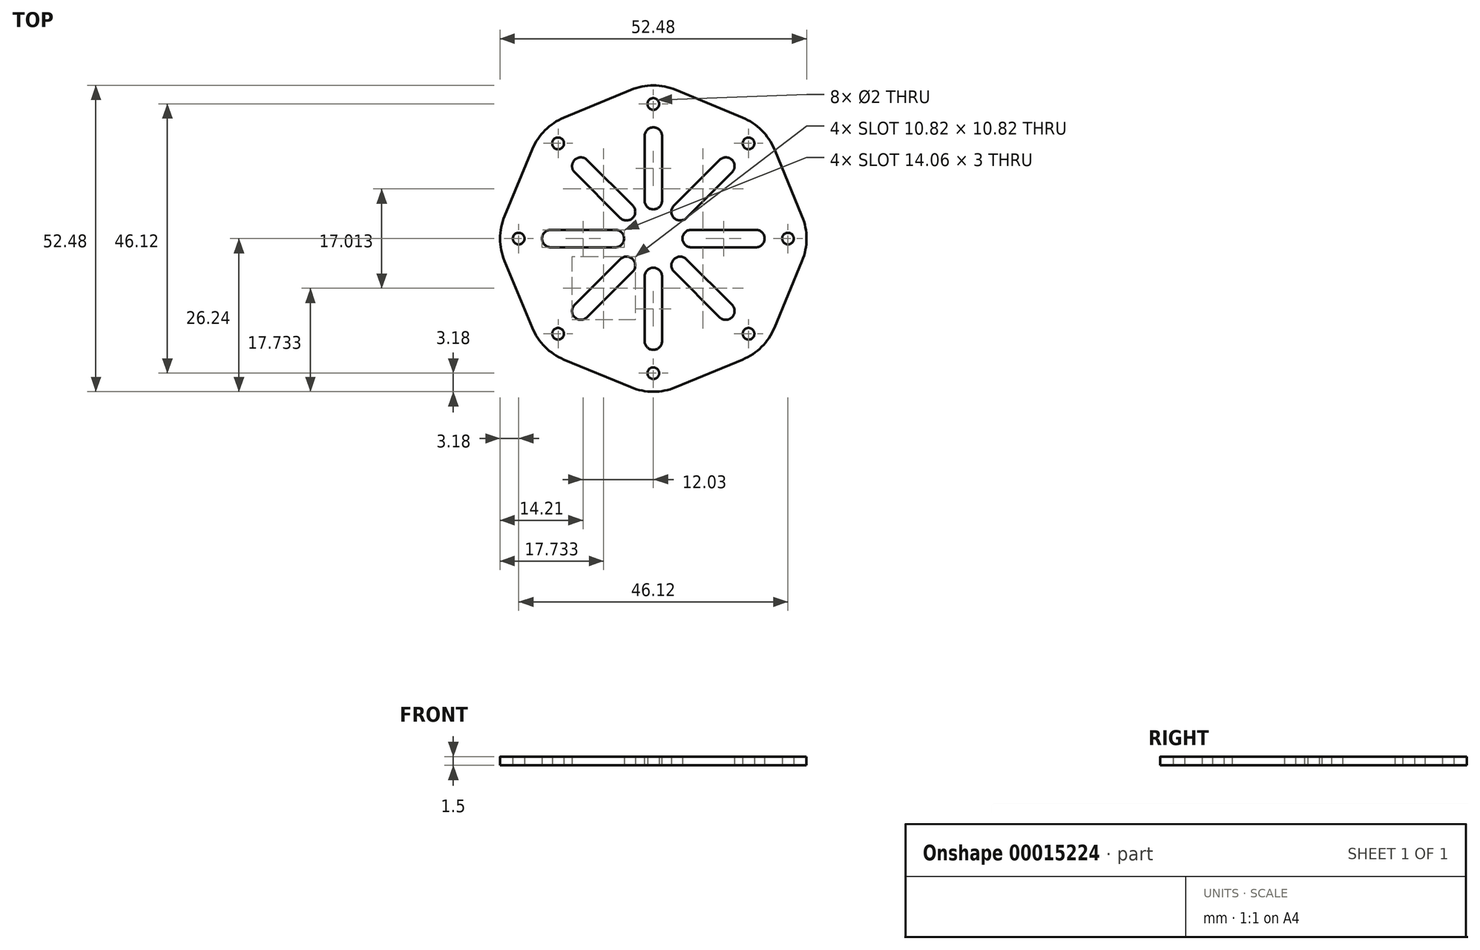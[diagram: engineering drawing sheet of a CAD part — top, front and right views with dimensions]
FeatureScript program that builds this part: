
annotation { "Feature Type Name" : "Feature", "Feature Type Description" : "" }
export const myFeature = defineFeature(function(context is Context, id is Id, definition is map)
    precondition{}
    {
        {
            var Q0;
            Q0=qCreatedBy(makeId("Top.planeOp"),FACE);
            var sketch = newSketch(context, id + "F0", { "sketchPlane" : qUnion([Q0])});
            skCircle(sketch, "E0.cCircle", {"center": v(0, 0) * mm, "radius": 25 * mm, "construction": true});
            skLineSegment(sketch, "E0.0", {"start": v(19.13, 19.13) * mm, "end": v(27.06, 0) * mm});
            skLineSegment(sketch, "E0.1", {"start": v(27.06, 0) * mm, "end": v(19.13, -19.13) * mm});
            skLineSegment(sketch, "E0.2", {"start": v(19.13, -19.13) * mm, "end": v(0, -27.06) * mm});
            skLineSegment(sketch, "E0.3", {"start": v(0, -27.06) * mm, "end": v(-19.13, -19.13) * mm});
            skLineSegment(sketch, "E0.4", {"start": v(-19.13, -19.13) * mm, "end": v(-27.06, 0) * mm});
            skLineSegment(sketch, "E0.5", {"start": v(-27.06, 0) * mm, "end": v(-19.13, 19.13) * mm});
            skLineSegment(sketch, "E0.6", {"start": v(-19.13, 19.13) * mm, "end": v(0, 27.06) * mm});
            skLineSegment(sketch, "E0.7", {"start": v(0, 27.06) * mm, "end": v(19.13, 19.13) * mm});
            skPoint(sketch, "E0.0.midPoint", {"position": v(23.1, 9.57) * mm});
            skPoint(sketch, "E1", {"position": v(0, -23.06) * mm});
            skPoint(sketch, "E2.1.0", {"position": v(16.3, -16.3) * mm});
            skPoint(sketch, "E2.2.0", {"position": v(23.06, 0) * mm});
            skPoint(sketch, "E2.3.0", {"position": v(16.3, 16.3) * mm});
            skPoint(sketch, "E2.4.0", {"position": v(0, 23.06) * mm});
            skPoint(sketch, "E2.5.0", {"position": v(-16.3, 16.3) * mm});
            skPoint(sketch, "E2.6.0", {"position": v(-23.06, 0) * mm});
            skPoint(sketch, "E2.7.0", {"position": v(-16.3, -16.3) * mm});
            skCircle(sketch, "E3", {"center": v(0, 0) * mm, "radius": 19.06 * mm});
            skLineSegment(sketch, "E4", {"start": v(0, 19.06) * mm, "end": v(0, 23.06) * mm, "construction": true});
            skLineSegment(sketch, "E5", {"start": v(0, 23.06) * mm, "end": v(0, 27.06) * mm, "construction": true});
            skCircle(sketch, "E6", {"center": v(0, 0) * mm, "radius": 5 * mm});
            skLineSegment(sketch, "E7", {"start": v(-13.48, -13.48) * mm, "end": v(-3.54, -3.54) * mm});
            skLineSegment(sketch, "E8", {"start": v(19.06, 0) * mm, "end": v(5, 0) * mm});
            skLineSegment(sketch, "E9", {"start": v(0, 19.06) * mm, "end": v(0, 5) * mm});
            skLineSegment(sketch, "E10", {"start": v(13.48, -13.48) * mm, "end": v(3.54, -3.54) * mm});
            skLineSegment(sketch, "E11.trimOffspring", {"start": v(3.54, 3.54) * mm, "end": v(13.48, 13.48) * mm});
            skLineSegment(sketch, "E12.trimOffspring", {"start": v(-5, 0) * mm, "end": v(-19.06, 0) * mm});
            skLineSegment(sketch, "E13.trimOffspring", {"start": v(-3.54, 3.54) * mm, "end": v(-13.48, 13.48) * mm});
            skLineSegment(sketch, "E14.trimOffspring", {"start": v(0, -5) * mm, "end": v(0, -19.06) * mm});
            skSolve(sketch);
        }
        {
            var Q0;
            Q0=makeQuery(id+"F0.imprint","IMPRINT",FACE,{"disambiguationData":[TD([[makeQuery(id+"F0.imprint","IMPRINT",EDGE,{"derivedFrom":sQuery(id+"F0.wireOp",EDGE,"E0.0")}),-1.0]])]});
            var Q1;
            {var subQ1=sQuery(id+"F0.wireOp",EDGE,"E7");Q1=makeQuery(id+"F0.imprint","IMPRINT",FACE,{"disambiguationData":[TD([[makeQuery(id+"F0.imprint","IMPRINT",EDGE,{"derivedFrom":subQ1}),1.0]])]});}
            var Q2;
            {var subQ1=sQuery(id+"F0.wireOp",EDGE,"E7");Q2=makeQuery(id+"F0.imprint","IMPRINT",FACE,{"disambiguationData":[TD([[makeQuery(id+"F0.imprint","IMPRINT",EDGE,{"derivedFrom":subQ1}),-1.0]])]});}
            var Q3;
            {var subQ1=sQuery(id+"F0.wireOp",EDGE,"E10");Q3=makeQuery(id+"F0.imprint","IMPRINT",FACE,{"disambiguationData":[TD([[makeQuery(id+"F0.imprint","IMPRINT",EDGE,{"derivedFrom":subQ1}),1.0]])]});}
            var Q4;
            {var subQ1=sQuery(id+"F0.wireOp",EDGE,"E8");Q4=makeQuery(id+"F0.imprint","IMPRINT",FACE,{"disambiguationData":[TD([[makeQuery(id+"F0.imprint","IMPRINT",EDGE,{"derivedFrom":subQ1}),1.0]])]});}
            var Q5;
            {var subQ1=sQuery(id+"F0.wireOp",EDGE,"E8");Q5=makeQuery(id+"F0.imprint","IMPRINT",FACE,{"disambiguationData":[TD([[makeQuery(id+"F0.imprint","IMPRINT",EDGE,{"derivedFrom":subQ1}),-1.0]])]});}
            var Q6;
            {var subQ1=sQuery(id+"F0.wireOp",EDGE,"E9");Q6=makeQuery(id+"F0.imprint","IMPRINT",FACE,{"disambiguationData":[TD([[makeQuery(id+"F0.imprint","IMPRINT",EDGE,{"derivedFrom":subQ1}),1.0]])]});}
            var Q7;
            {var subQ1=sQuery(id+"F0.wireOp",EDGE,"E9");Q7=makeQuery(id+"F0.imprint","IMPRINT",FACE,{"disambiguationData":[TD([[makeQuery(id+"F0.imprint","IMPRINT",EDGE,{"derivedFrom":subQ1}),-1.0]])]});}
            var Q8;
            {var subQ1=sQuery(id+"F0.wireOp",EDGE,"E12.trimOffspring");Q8=makeQuery(id+"F0.imprint","IMPRINT",FACE,{"disambiguationData":[TD([[makeQuery(id+"F0.imprint","IMPRINT",EDGE,{"derivedFrom":subQ1}),-1.0]])]});}
            var Q9;
            {var subQ0=sQuery(id+"F0.wireOp",EDGE,"E6");var subQ2=makeQuery(id+"F0.imprint","INTERSECT",VERTEX,{"derivedFrom":[subQ0,sQuery(id+"F0.wireOp",EDGE,"E8")]});Q9=makeQuery(id+"F0.imprint","IMPRINT",FACE,{"disambiguationData":[TD([[makeQuery(id+"F0.imprint","IMPRINT",EDGE,{"disambiguationData":[TD([[subQ2,-1.0]])],"derivedFrom":subQ0}),1.0]])]});}
            extrude(context, id + "F1", {"entities" : qUnion([Q0, Q1, Q2, Q3, Q4, Q5, Q6, Q7, Q8, Q9]), "depth" : 1.5 * mm});
        }
        {
            var Q0;
            Q0=sQuery(id+"F0.wireOp",VERTEX,"E2.5.0");
            var Q1;
            Q1=sQuery(id+"F0.wireOp",VERTEX,"E2.4.0");
            var Q2;
            Q2=sQuery(id+"F0.wireOp",VERTEX,"E2.3.0");
            var Q3;
            Q3=sQuery(id+"F0.wireOp",VERTEX,"E2.2.0");
            var Q4;
            Q4=sQuery(id+"F0.wireOp",VERTEX,"E2.1.0");
            var Q5;
            Q5=sQuery(id+"F0.wireOp",VERTEX,"E1");
            var Q6;
            Q6=sQuery(id+"F0.wireOp",VERTEX,"E2.7.0");
            var Q7;
            Q7=sQuery(id+"F0.wireOp",VERTEX,"E2.6.0");
            var Q8;
            Q8=makeQuery(id+"F1.opExtrude","SWEPT_BODY",BODY,{"disambiguationData":[OSD([sQuery(id+"F0.wireOp",EDGE,"E0.0"),sQuery(id+"F0.wireOp",EDGE,"E0.1"),sQuery(id+"F0.wireOp",EDGE,"E0.2"),sQuery(id+"F0.wireOp",EDGE,"E0.3"),sQuery(id+"F0.wireOp",EDGE,"E0.4"),sQuery(id+"F0.wireOp",EDGE,"E0.5"),sQuery(id+"F0.wireOp",EDGE,"E0.6"),sQuery(id+"F0.wireOp",EDGE,"E0.7")])]});
            hole(context, id + "F2", {"style" : HoleStyle.SIMPLE, "holeDiameter" : 2 * mm, "endStyle" : HoleEndStyle.THROUGH, "oppositeDirection" : true, "locations" : qUnion([Q0, Q1, Q2, Q3, Q4, Q5, Q6, Q7]), "scope" : qUnion([Q8])});
        }
        {
            var Q0;
            Q0=makeQuery(id+"F1.opExtrude","SWEPT_EDGE",EDGE,{"disambiguationData":[OSD([sQuery(id+"F0.wireOp",EDGE,"E0.3"),sQuery(id+"F0.wireOp",EDGE,"E0.4")])]});
            var Q1;
            Q1=makeQuery(id+"F1.opExtrude","SWEPT_EDGE",EDGE,{"disambiguationData":[OSD([sQuery(id+"F0.wireOp",EDGE,"E0.2"),sQuery(id+"F0.wireOp",EDGE,"E0.3")])]});
            var Q2;
            Q2=makeQuery(id+"F1.opExtrude","SWEPT_EDGE",EDGE,{"disambiguationData":[OSD([sQuery(id+"F0.wireOp",EDGE,"E0.1"),sQuery(id+"F0.wireOp",EDGE,"E0.2")])]});
            var Q3;
            Q3=makeQuery(id+"F1.opExtrude","SWEPT_EDGE",EDGE,{"disambiguationData":[OSD([sQuery(id+"F0.wireOp",EDGE,"E0.0"),sQuery(id+"F0.wireOp",EDGE,"E0.1")])]});
            var Q4;
            Q4=makeQuery(id+"F1.opExtrude","SWEPT_EDGE",EDGE,{"disambiguationData":[OSD([sQuery(id+"F0.wireOp",EDGE,"E0.0"),sQuery(id+"F0.wireOp",EDGE,"E0.7")])]});
            var Q5;
            Q5=makeQuery(id+"F1.opExtrude","SWEPT_EDGE",EDGE,{"disambiguationData":[OSD([sQuery(id+"F0.wireOp",EDGE,"E0.6"),sQuery(id+"F0.wireOp",EDGE,"E0.7")])]});
            var Q6;
            Q6=makeQuery(id+"F1.opExtrude","SWEPT_EDGE",EDGE,{"disambiguationData":[OSD([sQuery(id+"F0.wireOp",EDGE,"E0.5"),sQuery(id+"F0.wireOp",EDGE,"E0.6")])]});
            var Q7;
            Q7=makeQuery(id+"F1.opExtrude","SWEPT_EDGE",EDGE,{"disambiguationData":[OSD([sQuery(id+"F0.wireOp",EDGE,"E0.4"),sQuery(id+"F0.wireOp",EDGE,"E0.5")])]});
            fillet(context, id + "F3", {"entities" : qUnion([Q0, Q1, Q2, Q3, Q4, Q5, Q6, Q7]), "radius" : 10 * mm, "tangentPropagation" : true, "allowEdgeOverflow" : false});
        }
        {
            var Q0;
            Q0=sQuery(id+"F0.wireOp",EDGE,"E13.trimOffspring");
            var Q1;
            Q1=sQuery(id+"F0.wireOp",EDGE,"E12.trimOffspring");
            var Q2;
            Q2=sQuery(id+"F0.wireOp",EDGE,"E7");
            var Q3;
            Q3=sQuery(id+"F0.wireOp",EDGE,"E14.trimOffspring");
            var Q4;
            Q4=sQuery(id+"F0.wireOp",EDGE,"E10");
            var Q5;
            Q5=sQuery(id+"F0.wireOp",EDGE,"E8");
            var Q6;
            Q6=sQuery(id+"F0.wireOp",EDGE,"E11.trimOffspring");
            var Q7;
            Q7=sQuery(id+"F0.wireOp",EDGE,"E9");
            extrude(context, id + "F4", {"bodyType" : ToolBodyType.SURFACE, "surfaceEntities" : qUnion([Q0, Q1, Q2, Q3, Q4, Q5, Q6, Q7]), "endBound" : BoundingType.THROUGH_ALL, "depth" : 25 * mm});
        }
        {
            var Q0;
            Q0=makeQuery(id+"F4.opExtrude","SWEPT_FACE",FACE,{"disambiguationData":[OSD([sQuery(id+"F0.wireOp",EDGE,"E7")])]});
            var Q1;
            Q1=makeQuery(id+"F4.opExtrude","SWEPT_FACE",FACE,{"disambiguationData":[OSD([sQuery(id+"F0.wireOp",EDGE,"E11.trimOffspring")])]});
            extrude(context, id + "F5", {"entities" : qUnion([Q0, Q1]), "operationType" : NewBodyOperationType.REMOVE, "endBound" : BoundingType.SYMMETRIC, "oppositeDirection" : true, "depth" : 3 * mm});
        }
        {
            var Q0;
            Q0=makeQuery(id+"F4.opExtrude","SWEPT_FACE",FACE,{"disambiguationData":[OSD([sQuery(id+"F0.wireOp",EDGE,"E10")])]});
            var Q1;
            Q1=makeQuery(id+"F4.opExtrude","SWEPT_FACE",FACE,{"disambiguationData":[OSD([sQuery(id+"F0.wireOp",EDGE,"E13.trimOffspring")])]});
            extrude(context, id + "F6", {"entities" : qUnion([Q0, Q1]), "operationType" : NewBodyOperationType.REMOVE, "endBound" : BoundingType.SYMMETRIC, "oppositeDirection" : true, "depth" : 3 * mm});
        }
        {
            var Q0;
            Q0=makeQuery(id+"F4.opExtrude","SWEPT_FACE",FACE,{"disambiguationData":[OSD([sQuery(id+"F0.wireOp",EDGE,"E14.trimOffspring")])]});
            var Q1;
            Q1=makeQuery(id+"F4.opExtrude","SWEPT_FACE",FACE,{"disambiguationData":[OSD([sQuery(id+"F0.wireOp",EDGE,"E9")])]});
            extrude(context, id + "F7", {"entities" : qUnion([Q0, Q1]), "operationType" : NewBodyOperationType.REMOVE, "endBound" : BoundingType.SYMMETRIC, "oppositeDirection" : true, "depth" : 3 * mm});
        }
        {
            var Q0;
            Q0=makeQuery(id+"F4.opExtrude","SWEPT_FACE",FACE,{"disambiguationData":[OSD([sQuery(id+"F0.wireOp",EDGE,"E12.trimOffspring")])]});
            var Q1;
            Q1=makeQuery(id+"F4.opExtrude","SWEPT_FACE",FACE,{"disambiguationData":[OSD([sQuery(id+"F0.wireOp",EDGE,"E8")])]});
            extrude(context, id + "F8", {"entities" : qUnion([Q0, Q1]), "operationType" : NewBodyOperationType.REMOVE, "endBound" : BoundingType.SYMMETRIC, "oppositeDirection" : true, "depth" : 3 * mm});
        }
        {
            var Q0;
            Q0=makeQuery(id+"F6.boolean.opBoolean","COPY",EDGE,{"derivedFrom":makeQuery(id+"F6.opExtrude","CAP_EDGE",EDGE,{"disambiguationData":[OSD([sQuery(id+"F0.wireOp",VERTEX,"E13.trimOffspring.start")])],"isStart":true})});
            var Q1;
            Q1=makeQuery(id+"F6.boolean.opBoolean","COPY",EDGE,{"derivedFrom":makeQuery(id+"F6.opExtrude","CAP_EDGE",EDGE,{"disambiguationData":[OSD([sQuery(id+"F0.wireOp",VERTEX,"E13.trimOffspring.start")])],"isStart":false})});
            var Q2;
            Q2=makeQuery(id+"F7.boolean.opBoolean","COPY",EDGE,{"derivedFrom":makeQuery(id+"F7.opExtrude","CAP_EDGE",EDGE,{"disambiguationData":[OSD([sQuery(id+"F0.wireOp",VERTEX,"E9.end")])],"isStart":true})});
            var Q3;
            Q3=makeQuery(id+"F7.boolean.opBoolean","COPY",EDGE,{"derivedFrom":makeQuery(id+"F7.opExtrude","CAP_EDGE",EDGE,{"disambiguationData":[OSD([sQuery(id+"F0.wireOp",VERTEX,"E9.end")])],"isStart":false})});
            var Q4;
            Q4=makeQuery(id+"F5.boolean.opBoolean","COPY",EDGE,{"derivedFrom":makeQuery(id+"F5.opExtrude","CAP_EDGE",EDGE,{"disambiguationData":[OSD([sQuery(id+"F0.wireOp",VERTEX,"E11.trimOffspring.start")])],"isStart":false})});
            var Q5;
            Q5=makeQuery(id+"F8.boolean.opBoolean","COPY",EDGE,{"derivedFrom":makeQuery(id+"F8.opExtrude","CAP_EDGE",EDGE,{"disambiguationData":[OSD([sQuery(id+"F0.wireOp",VERTEX,"E8.end")])],"isStart":true})});
            var Q6;
            Q6=makeQuery(id+"F6.boolean.opBoolean","COPY",EDGE,{"derivedFrom":makeQuery(id+"F6.opExtrude","CAP_EDGE",EDGE,{"disambiguationData":[OSD([sQuery(id+"F0.wireOp",VERTEX,"E10.end")])],"isStart":true})});
            var Q7;
            Q7=makeQuery(id+"F7.boolean.opBoolean","COPY",EDGE,{"derivedFrom":makeQuery(id+"F7.opExtrude","CAP_EDGE",EDGE,{"disambiguationData":[OSD([sQuery(id+"F0.wireOp",VERTEX,"E14.trimOffspring.start")])],"isStart":false})});
            var Q8;
            Q8=makeQuery(id+"F5.boolean.opBoolean","COPY",EDGE,{"derivedFrom":makeQuery(id+"F5.opExtrude","CAP_EDGE",EDGE,{"disambiguationData":[OSD([sQuery(id+"F0.wireOp",VERTEX,"E7.end")])],"isStart":true})});
            var Q9;
            Q9=makeQuery(id+"F8.boolean.opBoolean","COPY",EDGE,{"derivedFrom":makeQuery(id+"F8.opExtrude","CAP_EDGE",EDGE,{"disambiguationData":[OSD([sQuery(id+"F0.wireOp",VERTEX,"E12.trimOffspring.start")])],"isStart":false})});
            var Q10;
            Q10=makeQuery(id+"F8.boolean.opBoolean","COPY",EDGE,{"derivedFrom":makeQuery(id+"F8.opExtrude","CAP_EDGE",EDGE,{"disambiguationData":[OSD([sQuery(id+"F0.wireOp",VERTEX,"E12.trimOffspring.start")])],"isStart":true})});
            var Q11;
            Q11=makeQuery(id+"F5.boolean.opBoolean","COPY",EDGE,{"derivedFrom":makeQuery(id+"F5.opExtrude","CAP_EDGE",EDGE,{"disambiguationData":[OSD([sQuery(id+"F0.wireOp",VERTEX,"E7.end")])],"isStart":false})});
            var Q12;
            Q12=makeQuery(id+"F7.boolean.opBoolean","COPY",EDGE,{"derivedFrom":makeQuery(id+"F7.opExtrude","CAP_EDGE",EDGE,{"disambiguationData":[OSD([sQuery(id+"F0.wireOp",VERTEX,"E14.trimOffspring.start")])],"isStart":true})});
            var Q13;
            Q13=makeQuery(id+"F6.boolean.opBoolean","COPY",EDGE,{"derivedFrom":makeQuery(id+"F6.opExtrude","CAP_EDGE",EDGE,{"disambiguationData":[OSD([sQuery(id+"F0.wireOp",VERTEX,"E10.end")])],"isStart":false})});
            var Q14;
            Q14=makeQuery(id+"F8.boolean.opBoolean","COPY",EDGE,{"derivedFrom":makeQuery(id+"F8.opExtrude","CAP_EDGE",EDGE,{"disambiguationData":[OSD([sQuery(id+"F0.wireOp",VERTEX,"E8.end")])],"isStart":false})});
            var Q15;
            Q15=makeQuery(id+"F5.boolean.opBoolean","COPY",EDGE,{"derivedFrom":makeQuery(id+"F5.opExtrude","CAP_EDGE",EDGE,{"disambiguationData":[OSD([sQuery(id+"F0.wireOp",VERTEX,"E11.trimOffspring.start")])],"isStart":true})});
            var Q16;
            Q16=makeQuery(id+"F6.boolean.opBoolean","COPY",EDGE,{"derivedFrom":makeQuery(id+"F6.opExtrude","CAP_EDGE",EDGE,{"disambiguationData":[OSD([sQuery(id+"F0.wireOp",VERTEX,"E13.trimOffspring.end")])],"isStart":true})});
            var Q17;
            Q17=makeQuery(id+"F7.boolean.opBoolean","COPY",EDGE,{"derivedFrom":makeQuery(id+"F7.opExtrude","CAP_EDGE",EDGE,{"disambiguationData":[OSD([sQuery(id+"F0.wireOp",VERTEX,"E9.start")])],"isStart":false})});
            var Q18;
            Q18=makeQuery(id+"F5.boolean.opBoolean","COPY",EDGE,{"derivedFrom":makeQuery(id+"F5.opExtrude","CAP_EDGE",EDGE,{"disambiguationData":[OSD([sQuery(id+"F0.wireOp",VERTEX,"E11.trimOffspring.end")])],"isStart":true})});
            var Q19;
            Q19=makeQuery(id+"F8.boolean.opBoolean","COPY",EDGE,{"derivedFrom":makeQuery(id+"F8.opExtrude","CAP_EDGE",EDGE,{"disambiguationData":[OSD([sQuery(id+"F0.wireOp",VERTEX,"E8.start")])],"isStart":false})});
            var Q20;
            Q20=makeQuery(id+"F6.boolean.opBoolean","COPY",EDGE,{"derivedFrom":makeQuery(id+"F6.opExtrude","CAP_EDGE",EDGE,{"disambiguationData":[OSD([sQuery(id+"F0.wireOp",VERTEX,"E10.start")])],"isStart":false})});
            var Q21;
            Q21=makeQuery(id+"F7.boolean.opBoolean","COPY",EDGE,{"derivedFrom":makeQuery(id+"F7.opExtrude","CAP_EDGE",EDGE,{"disambiguationData":[OSD([sQuery(id+"F0.wireOp",VERTEX,"E14.trimOffspring.end")])],"isStart":true})});
            var Q22;
            Q22=makeQuery(id+"F5.boolean.opBoolean","COPY",EDGE,{"derivedFrom":makeQuery(id+"F5.opExtrude","CAP_EDGE",EDGE,{"disambiguationData":[OSD([sQuery(id+"F0.wireOp",VERTEX,"E7.start")])],"isStart":false})});
            var Q23;
            Q23=makeQuery(id+"F8.boolean.opBoolean","COPY",EDGE,{"derivedFrom":makeQuery(id+"F8.opExtrude","CAP_EDGE",EDGE,{"disambiguationData":[OSD([sQuery(id+"F0.wireOp",VERTEX,"E12.trimOffspring.end")])],"isStart":true})});
            var Q24;
            Q24=makeQuery(id+"F6.boolean.opBoolean","COPY",EDGE,{"derivedFrom":makeQuery(id+"F6.opExtrude","CAP_EDGE",EDGE,{"disambiguationData":[OSD([sQuery(id+"F0.wireOp",VERTEX,"E13.trimOffspring.end")])],"isStart":false})});
            var Q25;
            Q25=makeQuery(id+"F8.boolean.opBoolean","COPY",EDGE,{"derivedFrom":makeQuery(id+"F8.opExtrude","CAP_EDGE",EDGE,{"disambiguationData":[OSD([sQuery(id+"F0.wireOp",VERTEX,"E12.trimOffspring.end")])],"isStart":false})});
            var Q26;
            Q26=makeQuery(id+"F5.boolean.opBoolean","COPY",EDGE,{"derivedFrom":makeQuery(id+"F5.opExtrude","CAP_EDGE",EDGE,{"disambiguationData":[OSD([sQuery(id+"F0.wireOp",VERTEX,"E7.start")])],"isStart":true})});
            var Q27;
            Q27=makeQuery(id+"F7.boolean.opBoolean","COPY",EDGE,{"derivedFrom":makeQuery(id+"F7.opExtrude","CAP_EDGE",EDGE,{"disambiguationData":[OSD([sQuery(id+"F0.wireOp",VERTEX,"E14.trimOffspring.end")])],"isStart":false})});
            var Q28;
            Q28=makeQuery(id+"F6.boolean.opBoolean","COPY",EDGE,{"derivedFrom":makeQuery(id+"F6.opExtrude","CAP_EDGE",EDGE,{"disambiguationData":[OSD([sQuery(id+"F0.wireOp",VERTEX,"E10.start")])],"isStart":true})});
            var Q29;
            Q29=makeQuery(id+"F8.boolean.opBoolean","COPY",EDGE,{"derivedFrom":makeQuery(id+"F8.opExtrude","CAP_EDGE",EDGE,{"disambiguationData":[OSD([sQuery(id+"F0.wireOp",VERTEX,"E8.start")])],"isStart":true})});
            var Q30;
            Q30=makeQuery(id+"F5.boolean.opBoolean","COPY",EDGE,{"derivedFrom":makeQuery(id+"F5.opExtrude","CAP_EDGE",EDGE,{"disambiguationData":[OSD([sQuery(id+"F0.wireOp",VERTEX,"E11.trimOffspring.end")])],"isStart":false})});
            var Q31;
            Q31=makeQuery(id+"F7.boolean.opBoolean","COPY",EDGE,{"derivedFrom":makeQuery(id+"F7.opExtrude","CAP_EDGE",EDGE,{"disambiguationData":[OSD([sQuery(id+"F0.wireOp",VERTEX,"E9.start")])],"isStart":true})});
            fillet(context, id + "F9", {"entities" : qUnion([Q0, Q1, Q2, Q3, Q4, Q5, Q6, Q7, Q8, Q9, Q10, Q11, Q12, Q13, Q14, Q15, Q16, Q17, Q18, Q19, Q20, Q21, Q22, Q23, Q24, Q25, Q26, Q27, Q28, Q29, Q30, Q31]), "radius" : 1.5 * mm, "tangentPropagation" : true, "allowEdgeOverflow" : false});
        }
    });
